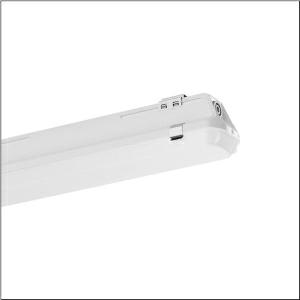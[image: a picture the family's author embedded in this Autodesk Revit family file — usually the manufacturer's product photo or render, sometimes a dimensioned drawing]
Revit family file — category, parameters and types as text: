
# Revit family: monsun_r__11_emergency_51fp207p437h3g_0ff0
name_source: partatom
category: Lighting Fixtures
units: mm (PartAtom-declared; Revit-internal decimal feet)

## family parameters
Cut with Voids When Loaded = No
Host = Face
Light Source = No
Part Type = Normal
Room Calculation Point = No
Round Connector Dimension = Use Diameter
Shared = No

## types (1)
- Monsun® 11 emergency (1 x LED, 3990 lm, 27.5 W, 4000K)
    Apparent Load = 28 VA
    CIE Flux Codes = 45 75 93 94 100
    Color Rendering = 80
    Color Temperature = 4000K
    Default Elevation = 1800 mm
    Description = Monsun® 11 emergency, damp-proof luminaire, chain hanger, primary optical cover: enclosure, of PC, light emission: direct distribution, primary light characteristic: symmetric, installation type: suspended mounting, surface-mounted, horizontal mounting, vertical mounting, LED, rated luminous flux: 3.990lm, luminous efficacy: 145lm/W, light colour: 840, colour temperature: 4000K, control gear: ECG, with terminal, 4-pole, max. 2.5mm², mains connection: 220..240V, AC, 50/60Hz, rated input power: 28W, control gear: single battery element, battery: NiCd, 4,5Ah, mains connection: 230V, luminaire housing, of glass-fibre reinforced polyester, uncoated, bright grey, incl. chain hanger, length: 1.590mm, width: 90mm, height: 88mm, clip for enclosure, of stainless steel (V2A), ceiling mounting element, of stainless steel (V2A), chain hanger, of stainless steel (V2A), protection rating (complete): IP66, insulation class (complete): insulation class I (protective earthing), certification: CE, UKCA, protection symbol: D, impact resistance: IK08, permissible operating ambient temperature: +5..+35°C, standard: EN 50419, EN 60598-2-1, EN 60598-2-22, no direct snow, no direct sun, no direct rain, for indoor or canopied outdoor use, corresponds to IFS (International Featured Standards) requirements for safety and quality in the food industry, contact your sales advisor before using the luminaires in applications with unclear chemical exposure, large temperature fluctuations or condensation-forming humidity, LABS conformity tested according to VDMA 24364:2018-05, packaging unit: 1 piece
    Height = 89 mm
    Lamp = 1 x LED
    Lamp Light Flux = 3990 lm
    Lamp Power = 27.5 W
    Lamp count = 1
    Length = 1590 mm
    Luminous efficacy = 145 lm/W
    Manufacturer = Siteco
    ModVariant = No
    Model = 51FP207P437H3G
    Mounting Place = Ceiling
    Mounting Type = Surface mounted
    Number of Poles = 1
    OnlyDefault = Yes
    Power Factor = 1
    Product Name = Monsun® 11 emergency
    Product group = damp-proof luminaire
    ProductGroupID = 300
    Protection Class = Protection class I
    Protection Degree = IP 66
    RLX_Detail_Level = 1
    RLX_Emergency_Light_Flux = 0 lm
    RLX_Emergency_Type = 0
    RLX_Emergency_Type_DB = No
    RlxData = <blob elided: 89129 chars, md5=b4b8ca5d>
    Socket = socket
    Standby Power = 0 W
    System Light Flux = 3990 lm
    System Power = 28 W
    Type Comments = Product without accessories
    Type Image = l_1004748.jpg
    URL = http://relux.com
    VarID = ---
    Voltage = 0 V
    Weight = 0.00 kg
    Width = 90 mm

## geometry (parser evidence)
native form markers: Blend x4, Sweep x13
no freeform markers — native parametric forms only
